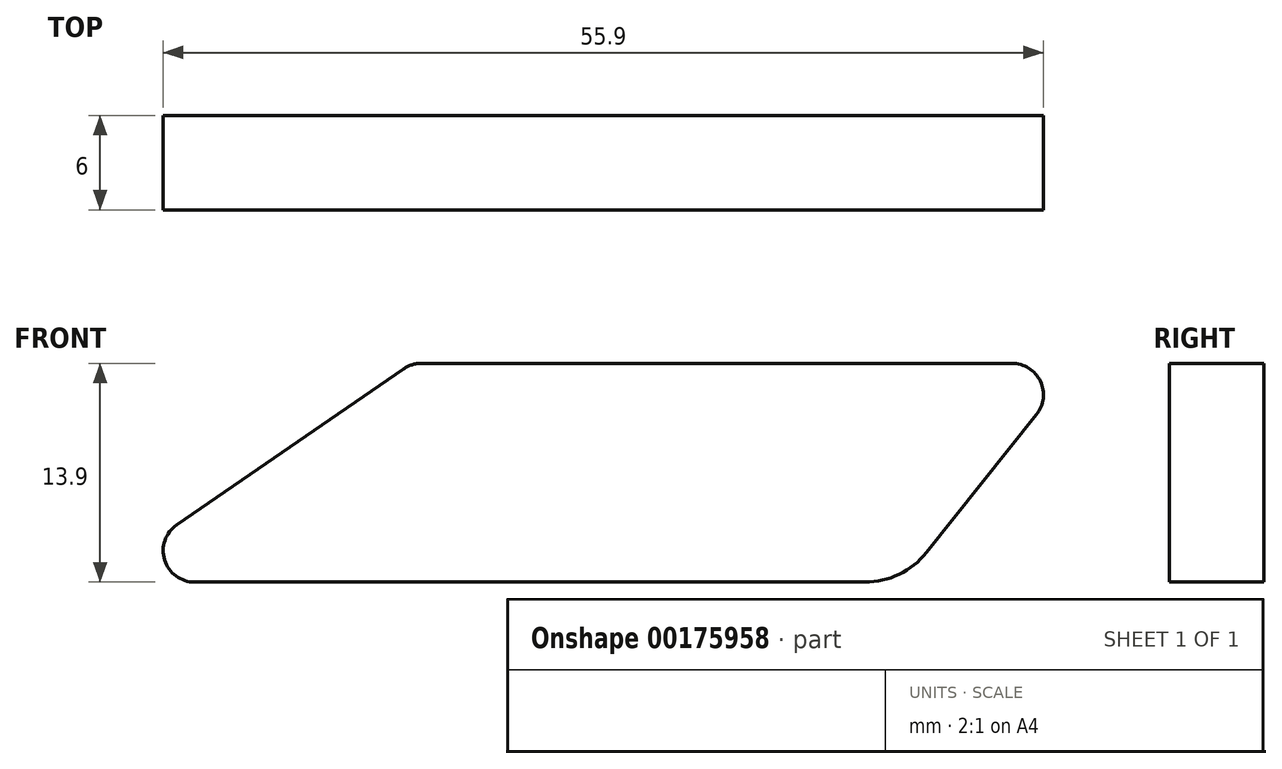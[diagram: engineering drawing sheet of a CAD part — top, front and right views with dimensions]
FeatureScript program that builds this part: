
annotation { "Feature Type Name" : "Feature", "Feature Type Description" : "" }
export const myFeature = defineFeature(function(context is Context, id is Id, definition is map)
    precondition{}
    {
        {
            var Q0;
            Q0=qCreatedBy(makeId("Front.planeOp"),FACE);
            var sketch = newSketch(context, id + "F0", { "sketchPlane" : qUnion([Q0])});
            skLineSegment(sketch, "E0", {"start": v(21.73, 10.65) * mm, "end": v(14.74, 1.88) * mm});
            skLineSegment(sketch, "E1", {"start": v(10.83, 0) * mm, "end": v(-31.74, 0) * mm});
            skLineSegment(sketch, "E2", {"start": v(-32.88, 3.65) * mm, "end": v(-18.48, 13.55) * mm});
            skLineSegment(sketch, "E3", {"start": v(-17.35, 13.9) * mm, "end": v(20.16, 13.9) * mm});
            skPoint(sketch, "E4.visualSharp", {"position": v(-17.97, 13.9) * mm});
            skArc(sketch, "E4.filletArc", {"start": v(-17.35, 13.9) * mm, "mid": v(-17.94, 13.8) * mm, "end": v(-18.48, 13.55) * mm});
            skPoint(sketch, "E5.visualSharp", {"position": v(13.24, 0) * mm});
            skArc(sketch, "E5.filletArc", {"start": v(10.83, 0) * mm, "mid": v(13, 0.5) * mm, "end": v(14.74, 1.88) * mm});
            skPoint(sketch, "E6.visualSharp", {"position": v(24.32, 13.9) * mm});
            skArc(sketch, "E6.filletArc", {"start": v(21.73, 10.65) * mm, "mid": v(21.96, 12.76) * mm, "end": v(20.16, 13.9) * mm});
            skPoint(sketch, "E7.visualSharp", {"position": v(-38.18, 0) * mm});
            skArc(sketch, "E7.filletArc", {"start": v(-32.88, 3.65) * mm, "mid": v(-33.65, 1.4) * mm, "end": v(-31.74, 0) * mm});
            skSolve(sketch);
        }
        {
            var Q0;
            Q0 = qSketchRegion(id + "F0", true);
            extrude(context, id + "F1", {"entities" : qUnion([Q0]), "depth" : 6 * mm});
        }
    });
